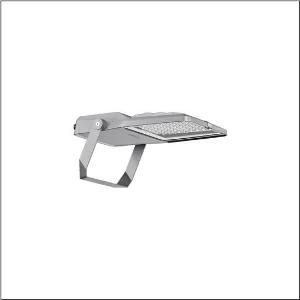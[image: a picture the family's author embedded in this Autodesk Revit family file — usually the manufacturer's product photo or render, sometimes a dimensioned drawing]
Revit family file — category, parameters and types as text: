
# Revit family: floodlight_fl_21_mini___pl64_5xa7776d2e1a_08ea
name_source: partatom
category: Lighting Fixtures
units: mm (PartAtom-declared; Revit-internal decimal feet)

## family parameters
Cut with Voids When Loaded = No
Host = Face
Light Source = No
Part Type = Normal
Room Calculation Point = No
Round Connector Dimension = Use Diameter
Shared = No

## types (1)
- --- (1 x LED, 17220 lm, 142.9 W, 3000K)
    Apparent Load = 143 VA
    CIE Flux Codes = 28 80 98 100 100
    Color Rendering = 70
    Color Temperature = 3000K
    Default Elevation = 1800 mm
    Description = Floodlight FL 21 mini, floodlight, primary light control with lens, of PMMA, primary optical cover: protective disc, of toughened safety glass, transparent, light distribution: PL64, light emission: direct distribution, installation type: surface-mounted, LED, High Power LED, rated luminous flux: 17.220lm, luminous efficacy: 121lm/W, light colour: 730, colour temperature: 3000K, control: flexible luminous flux parameterisation, time-dependent luminous flux control, constant luminous flux control, overheat protection, presetting dimming logarithmic, with terminal, 6-pole, mains connection: 220..240V, AC, 50/60Hz, start of lifetime: 143W, end of service life: 151W, reduction: 63W, luminaire housing, of diecast aluminium, powder-coated, Siteco® metallic grey (DB 702S), corrosivity category C5 mid according to DIN EN ISO 12944, sealing non-destructively replaceable, mounting bracket, of steel, galvanised, powder-coated, Siteco® metallic grey (DB 702S), Smart Interface below and above, protection rating (complete): IP66, insulation class (complete): insulation class II (safety insulation), certification: CE, ENEC, VDE, protection symbol: D, impact resistance: IK08, permissible operating ambient temperature: -40..+40°C, permissible operating ambient temperature for outdoor applications: -40..+50°C, standard: DIN EN 12944, LABS conformity tested according to VDMA 24364:2018-05, packaging unit: 1 piece

Light Distribution: PL64
    Height = 70 mm
    Lamp = 1 x LED
    Lamp Light Flux = 17220 lm
    Lamp Power = 142.9 W
    Lamp count = 1
    Length = 485 mm
    Luminous efficacy = 121 lm/W
    Manufacturer = Siteco
    ModVariant = No
    Model = 5XA7776D2E1A
    Number of Poles = 1
    OnlyDefault = Yes
    Power Factor = 1
    Product Name = Floodlight FL 21 mini | PL64
    Product group = floodlight | pylon annexe
    ProductGroupID = 6200
    Protection Class = Protection class II
    Protection Degree = IP 66
    RLX_Detail_Level = 1
    RLX_Emergency_Light_Flux = 0 lm
    RLX_Emergency_Type = 0
    RLX_Emergency_Type_DB = No
    RlxData = <blob elided: 96321 chars, md5=142dcb97>
    Socket = socket
    Standby Power = 0 W
    System Light Flux = 17220 lm
    System Power = 143 W
    Type Comments = factory setting: luminous flux: 100 % | dim-lin: 254 | 730 mA
    Type Image = l_1006845.jpg
    URL = http://relux.com
    VarID = @adj_115391
    Voltage = 0 V
    Weight = 0.00 kg
    Width = 337 mm

## geometry (parser evidence)
native form markers: Blend x4, Sweep x10
no freeform markers — native parametric forms only
